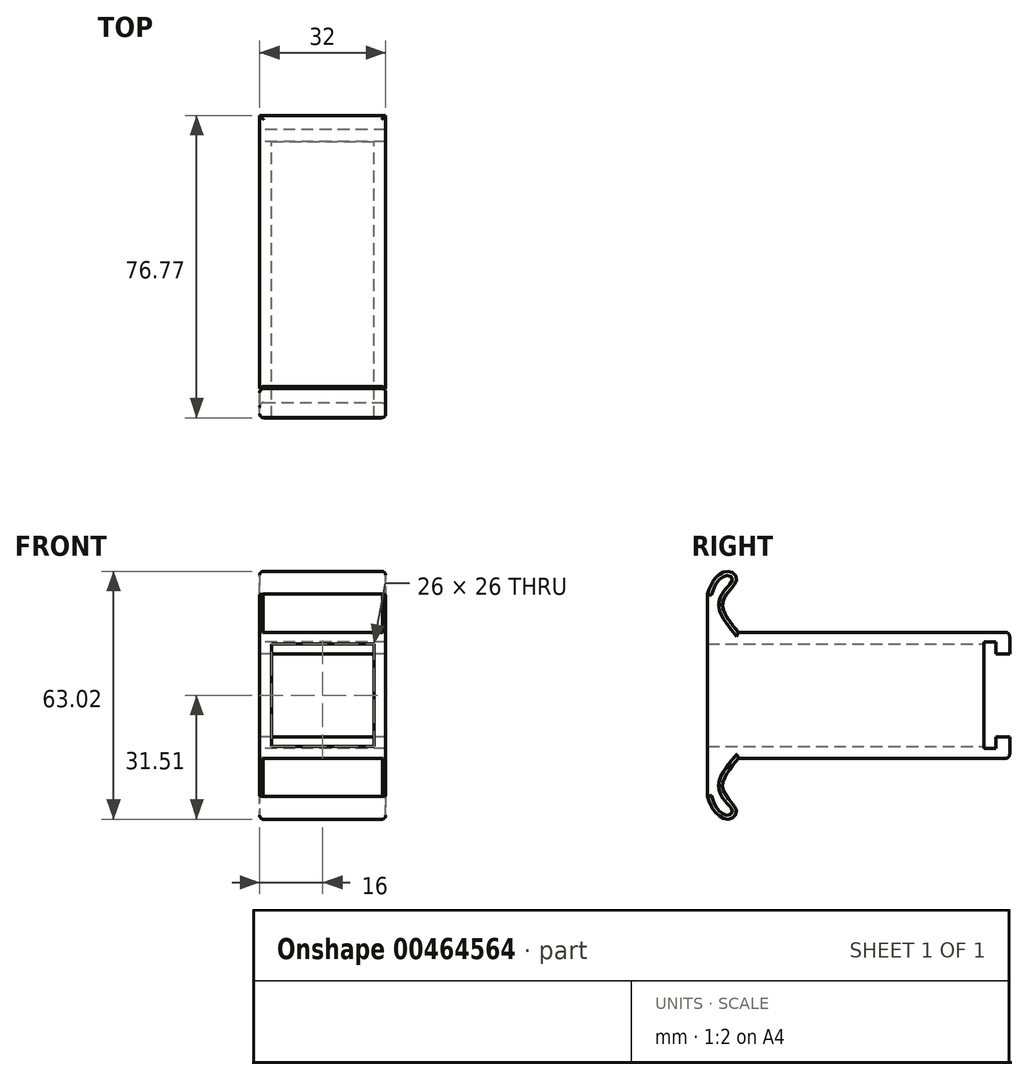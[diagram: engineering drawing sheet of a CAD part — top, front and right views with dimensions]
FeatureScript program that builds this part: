
annotation { "Feature Type Name" : "Feature", "Feature Type Description" : "" }
export const myFeature = defineFeature(function(context is Context, id is Id, definition is map)
    precondition{}
    {
        {
            var Q0;
            Q0=qCreatedBy(makeId("Front.planeOp"),FACE);
            var sketch = newSketch(context, id + "F0", { "sketchPlane" : qUnion([Q0])});
            skPoint(sketch, "E0.middle", {"position": v(0, 0) * mm});
            skLineSegment(sketch, "E1.bottom", {"start": v(16, 16) * mm, "end": v(-16, 16) * mm});
            skLineSegment(sketch, "E1.top", {"start": v(16, -16) * mm, "end": v(-16, -16) * mm});
            skLineSegment(sketch, "E1.left", {"start": v(16, 16) * mm, "end": v(16, -16) * mm});
            skLineSegment(sketch, "E1.right", {"start": v(-16, 16) * mm, "end": v(-16, -16) * mm});
            skSolve(sketch);
        }
        {
            var Q0;
            Q0 = qSketchRegion(id + "F0", true);
            var Q1;
            Q1 = qSketchRegion(id + "F7", true);
            extrude(context, id + "F1", {"entities" : qUnion([Q0, Q1]), "depth" : 80 * mm});
        }
        {
            var Q0;
            Q0=makeQuery(id+"F1.opExtrude","CAP_FACE",FACE,{"disambiguationData":[OSD([sQuery(id+"F0.wireOp",EDGE,"E1.bottom"),sQuery(id+"F0.wireOp",EDGE,"E1.top"),sQuery(id+"F0.wireOp",EDGE,"E1.left"),sQuery(id+"F0.wireOp",EDGE,"E1.right")])],"isStart":false});
            var Q1;
            Q1=makeQuery(id+"F1.opExtrude","CAP_FACE",FACE,{"disambiguationData":[OSD([sQuery(id+"F0.wireOp",EDGE,"E1.bottom"),sQuery(id+"F0.wireOp",EDGE,"E1.top"),sQuery(id+"F0.wireOp",EDGE,"E1.left"),sQuery(id+"F0.wireOp",EDGE,"E1.right")])],"isStart":true});
            shell(context, id + "F2", {"entities" : qUnion([Q0, Q1]), "thickness" : 3 * mm});
        }
        {
            var Q0;
            Q0=qCreatedBy(makeId("Right.planeOp"),FACE);
            var sketch = newSketch(context, id + "F3", { "sketchPlane" : qUnion([Q0])});
            skLineSegment(sketch, "E2.bottom", {"start": v(-3.5, 13.55) * mm, "end": v(-6.6, 13.55) * mm});
            skLineSegment(sketch, "E2.top", {"start": v(-3.5, -13.55) * mm, "end": v(-6.6, -13.55) * mm});
            skLineSegment(sketch, "E2.right", {"start": v(-6.6, 13.55) * mm, "end": v(-6.6, -13.55) * mm});
            skPoint(sketch, "E2.middle", {"position": v(-5.05, 0) * mm});
            skLineSegment(sketch, "E3", {"start": v(-3.5, 13.55) * mm, "end": v(-3.5, 10.55) * mm});
            skLineSegment(sketch, "E4", {"start": v(0, 10.55) * mm, "end": v(0, 0) * mm});
            skLineSegment(sketch, "E5.MirrorCS", {"start": v(-3.5, -13.55) * mm, "end": v(-3.5, -10.55) * mm});
            skLineSegment(sketch, "E6", {"start": v(-3.5, 10.55) * mm, "end": v(0, 10.55) * mm});
            skLineSegment(sketch, "E7.MirrorCS", {"start": v(-3.5, -10.55) * mm, "end": v(0, -10.55) * mm});
            skLineSegment(sketch, "E8.MirrorCS", {"start": v(0, -10.55) * mm, "end": v(0, 0) * mm});
            skLineSegment(sketch, "E9", {"start": v(-80, 27.8) * mm, "end": v(-80, -30.8) * mm});
            skLineSegment(sketch, "E10", {"start": v(-76.77, -30.8) * mm, "end": v(-76.77, 27.8) * mm});
            skLineSegment(sketch, "E11", {"start": v(-76.77, 27.8) * mm, "end": v(-80, 27.8) * mm});
            skLineSegment(sketch, "E12", {"start": v(-80, -30.8) * mm, "end": v(-76.77, -30.8) * mm});
            skSolve(sketch);
        }
        {
            var Q0;
            Q0 = qSketchRegion(id + "F3", true);
            extrude(context, id + "F4", {"entities" : qUnion([Q0]), "operationType" : NewBodyOperationType.REMOVE, "depth" : 25 * mm, "hasSecondDirection" : true, "secondDirectionOppositeDirection" : true, "secondDirectionDepth" : 25 * mm});
        }
        {
            var Q0;
            Q0=qCreatedBy(makeId("Right.planeOp"),FACE);
            var sketch = newSketch(context, id + "F5", { "sketchPlane" : qUnion([Q0])});
            skLineSegment(sketch, "E13.bottom", {"start": v(0, 10.55) * mm, "end": v(-3.5, 10.55) * mm});
            skLineSegment(sketch, "E13.top", {"start": v(0, 14.55) * mm, "end": v(-3.5, 14.55) * mm});
            skLineSegment(sketch, "E13.left", {"start": v(0, 10.55) * mm, "end": v(0, 14.55) * mm});
            skLineSegment(sketch, "E13.right", {"start": v(-3.5, 10.55) * mm, "end": v(-3.5, 14.55) * mm});
            skLineSegment(sketch, "E14.MirrorCS", {"start": v(0, -14.55) * mm, "end": v(-3.5, -14.55) * mm});
            skLineSegment(sketch, "E15.MirrorCS", {"start": v(-3.5, -10.55) * mm, "end": v(-3.5, -14.55) * mm});
            skLineSegment(sketch, "E16.MirrorCS", {"start": v(0, -10.55) * mm, "end": v(0, -14.55) * mm});
            skLineSegment(sketch, "E17.MirrorCS", {"start": v(0, -10.55) * mm, "end": v(-3.5, -10.55) * mm});
            skSolve(sketch);
        }
        {
            var Q0;
            Q0 = qSketchRegion(id + "F5", true);
            extrude(context, id + "F6", {"entities" : qUnion([Q0]), "operationType" : NewBodyOperationType.ADD, "depth" : 16 * mm, "hasSecondDirection" : true, "secondDirectionOppositeDirection" : true, "secondDirectionDepth" : 16 * mm});
        }
        {
            var Q0;
            Q0=qCreatedBy(makeId("Right.planeOp"),FACE);
            var sketch = newSketch(context, id + "F7", { "sketchPlane" : qUnion([Q0])});
            skPoint(sketch, "E18", {"position": v(-76.85, 0) * mm});
            skLineSegment(sketch, "E19", {"start": v(-76.75, 16) * mm, "end": v(-76.75, 25.71) * mm});
            skFitSpline(sketch, "E20", {"points": [v(-76.75, 25.71) * mm, v(-75.14, 29.31) * mm, v(-71.54, 31.5) * mm, v(-69.35, 29.63) * mm, v(-71.9, 25.71) * mm, v(-72.8, 21.95) * mm, v(-68.88, 16) * mm], "startDerivative": vector(8, 23.15) * mm, "endDerivative": vector(24.07, -29.13) * mm});
            skLineSegment(sketch, "E21", {"start": v(-76.75, 16) * mm, "end": v(-68.88, 16) * mm});
            skLineSegment(sketch, "E22.MirrorCS", {"start": v(-76.75, -16) * mm, "end": v(-76.75, -25.71) * mm});
            skFitSpline(sketch, "E23.MirrorCS", {"points": [v(-76.75, -25.71) * mm, v(-75.14, -29.31) * mm, v(-71.54, -31.5) * mm, v(-69.35, -29.63) * mm, v(-71.9, -25.71) * mm, v(-72.8, -21.95) * mm, v(-68.88, -16) * mm], "startDerivative": vector(8, -23.15) * mm, "endDerivative": vector(24.07, 29.13) * mm});
            skLineSegment(sketch, "E24.MirrorCS", {"start": v(-76.75, -16) * mm, "end": v(-68.88, -16) * mm});
            skSolve(sketch);
        }
        {
            var Q0;
            Q0 = qSketchRegion(id + "F7", true);
            extrude(context, id + "F8", {"entities" : qUnion([Q0]), "operationType" : NewBodyOperationType.ADD, "depth" : 16 * mm, "hasSecondDirection" : true, "secondDirectionOppositeDirection" : true, "secondDirectionDepth" : 16 * mm});
        }
        {
            var Q0;
            {var subQ0=sQuery(id+"F0.wireOp",EDGE,"E1.left");var subQ1=sQuery(id+"F0.wireOp",EDGE,"E1.bottom");Q0=makeQuery(id+"F8.boolean.opBoolean","SPLIT",EDGE,{"disambiguationData":[TD([makeQuery(id+"F6.opExtrude","SWEPT_FACE",FACE,{"disambiguationData":[OSD([sQuery(id+"F5.wireOp",EDGE,"E13.left")])]})])],"derivedFrom":makeQuery(id+"F1.opExtrude","SWEPT_EDGE",EDGE,{"disambiguationData":[OSD([subQ1,subQ0])]})});}
            var Q1;
            {var subQ0=sQuery(id+"F0.wireOp",EDGE,"E1.right");var subQ1=sQuery(id+"F0.wireOp",EDGE,"E1.bottom");Q1=makeQuery(id+"F8.boolean.opBoolean","SPLIT",EDGE,{"disambiguationData":[TD([makeQuery(id+"F6.opExtrude","SWEPT_FACE",FACE,{"disambiguationData":[OSD([sQuery(id+"F5.wireOp",EDGE,"E13.left")])]})])],"derivedFrom":makeQuery(id+"F1.opExtrude","SWEPT_EDGE",EDGE,{"disambiguationData":[OSD([subQ1,subQ0])]})});}
            var Q2;
            Q2=makeQuery(id+"F8.opExtrude","CAP_EDGE",EDGE,{"disambiguationData":[OSD([sQuery(id+"F7.wireOp",EDGE,"E20")])],"isStart":false});
            var Q3;
            Q3=makeQuery(id+"F8.opExtrude","CAP_EDGE",EDGE,{"disambiguationData":[OSD([sQuery(id+"F7.wireOp",EDGE,"E20")])],"isStart":true});
            var Q4;
            Q4=makeQuery(id+"F4.boolean.opBoolean","INTERSECT",EDGE,{"derivedFrom":[makeQuery(id+"F1.opExtrude","SWEPT_FACE",FACE,{"disambiguationData":[OSD([sQuery(id+"F0.wireOp",EDGE,"E1.left")])]}),makeQuery(id+"F4.opExtrude","SWEPT_FACE",FACE,{"disambiguationData":[OSD([sQuery(id+"F3.wireOp",EDGE,"E10")])]})]});
            var Q5;
            {var subQ0=sQuery(id+"F0.wireOp",EDGE,"E1.left");var subQ1=sQuery(id+"F0.wireOp",EDGE,"E1.top");Q5=makeQuery(id+"F8.boolean.opBoolean","SPLIT",EDGE,{"disambiguationData":[TD([makeQuery(id+"F6.opExtrude","SWEPT_FACE",FACE,{"disambiguationData":[OSD([sQuery(id+"F5.wireOp",EDGE,"E16.MirrorCS")])]})])],"derivedFrom":makeQuery(id+"F1.opExtrude","SWEPT_EDGE",EDGE,{"disambiguationData":[OSD([subQ1,subQ0])]})});}
            var Q6;
            Q6=makeQuery(id+"F8.opExtrude","CAP_EDGE",EDGE,{"disambiguationData":[OSD([sQuery(id+"F7.wireOp",EDGE,"E23.MirrorCS")])],"isStart":false});
            var Q7;
            Q7=makeQuery(id+"F1.opExtrude","CAP_EDGE",EDGE,{"disambiguationData":[OSD([sQuery(id+"F0.wireOp",EDGE,"E1.bottom")])],"isStart":true});
            var Q8;
            Q8=makeQuery(id+"F1.opExtrude","CAP_EDGE",EDGE,{"disambiguationData":[OSD([sQuery(id+"F0.wireOp",EDGE,"E1.top")])],"isStart":true});
            var Q9;
            {var subQ0=sQuery(id+"F0.wireOp",EDGE,"E1.right");var subQ1=sQuery(id+"F0.wireOp",EDGE,"E1.top");Q9=makeQuery(id+"F8.boolean.opBoolean","SPLIT",EDGE,{"disambiguationData":[TD([makeQuery(id+"F6.opExtrude","SWEPT_FACE",FACE,{"disambiguationData":[OSD([sQuery(id+"F5.wireOp",EDGE,"E16.MirrorCS")])]})])],"derivedFrom":makeQuery(id+"F1.opExtrude","SWEPT_EDGE",EDGE,{"disambiguationData":[OSD([subQ1,subQ0])]})});}
            var Q10;
            Q10=makeQuery(id+"F8.opExtrude","CAP_EDGE",EDGE,{"disambiguationData":[OSD([sQuery(id+"F7.wireOp",EDGE,"E23.MirrorCS")])],"isStart":true});
            var Q11;
            Q11=makeQuery(id+"F4.boolean.opBoolean","INTERSECT",EDGE,{"derivedFrom":[makeQuery(id+"F1.opExtrude","SWEPT_FACE",FACE,{"disambiguationData":[OSD([sQuery(id+"F0.wireOp",EDGE,"E1.right")])]}),makeQuery(id+"F4.opExtrude","SWEPT_FACE",FACE,{"disambiguationData":[OSD([sQuery(id+"F3.wireOp",EDGE,"E10")])]})]});
            fillet(context, id + "F9", {"entities" : qUnion([Q0, Q1, Q2, Q3, Q4, Q5, Q6, Q7, Q8, Q9, Q10, Q11]), "radius" : 1 * mm, "tangentPropagation" : true, "allowEdgeOverflow" : false});
        }
    });
